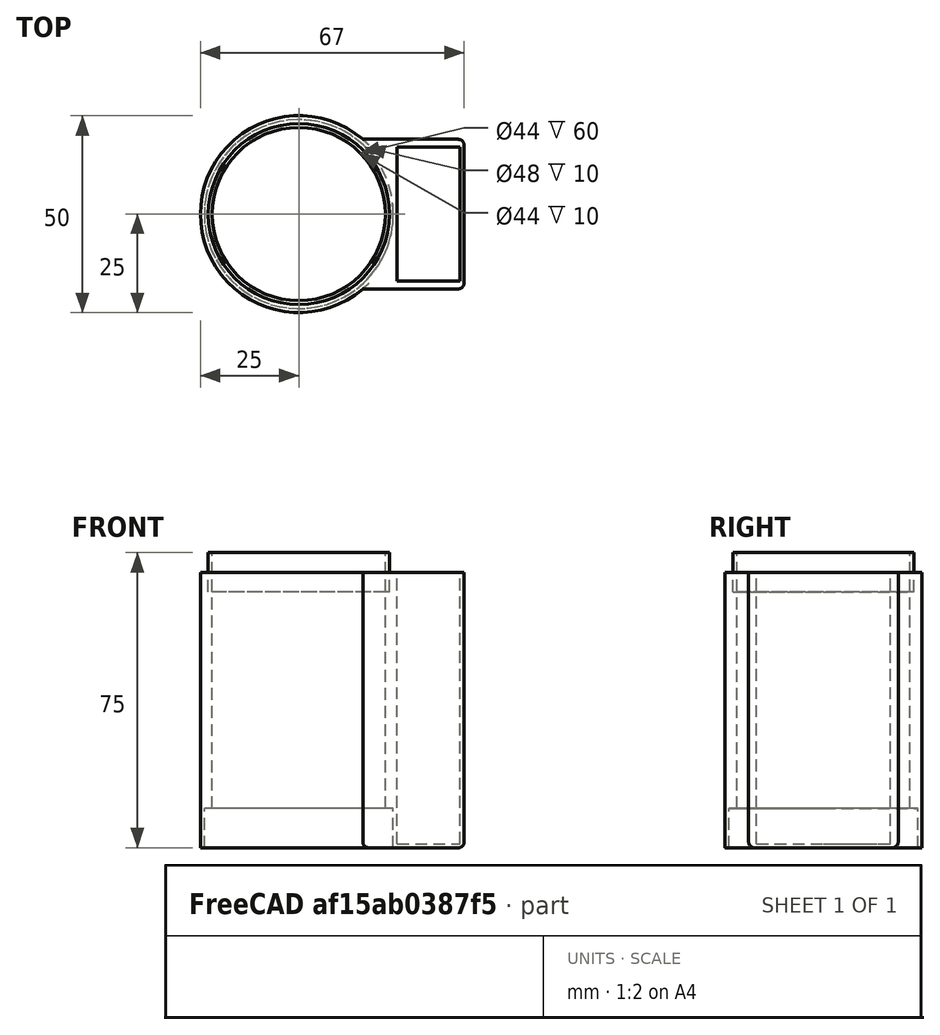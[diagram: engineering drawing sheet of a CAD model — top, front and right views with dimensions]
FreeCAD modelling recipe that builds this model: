
FCSTD DOCUMENT  (FreeCAD 0.15R4671 (Git))
Label: Mid section
License: CC-BY 3.0
LicenseURL: http://creativecommons.org/licenses/by/3.0/
objects: Part::Cylinder×5, Part::Cut×4, Part::Box×2, App::MeasureDistance×1, Part::Fillet×1, Part::MultiFuse×1
note: 13 computed .brp shape members not serialized (recipe doc carries the construction recipe); baked Part::Feature solids carry a one-line shape summary decoded from their .brp

FEATURE [Part::Cylinder] Cylinder  label="Cilindro"
  Angle = 360
  Height = 70
  Radius = 25
FEATURE [Part::Cylinder] Cylinder001  label="Cilindro001"
  Angle = 360
  Height = 78
  Radius = 22
FEATURE [Part::Cylinder] Cylinder003  label="Cilindro003"
  Angle = 360
  Height = 10
  Radius = 24
FEATURE [Part::Cylinder] Cylinder005  label="Cilindro005"
  Angle = 360
  Height = 21
  Radius = 22
FEATURE [Part::Cylinder] Cylinder006  label="Cilindro006"
  Angle = 360
  Height = 10
  Radius = 23
FEATURE [App::MeasureDistance] Distance  label="Distance: 70.087"
  Distance = 70.0868
  P1 = (-17.9835,17.3665,70)
  P2 = (-20.2254,14.6946,0)
FEATURE [Part::Box] Box  label="Cubo"
  Height = 70
  Length = 16
  Placement = pos=(25,-17,1) rot=(0,0,1;0rad)
  Width = 34
FEATURE [Part::Box] Box001  label="Cubo001"
  Height = 70
  Length = 26
  Placement = pos=(16,-19,0) rot=(0,0,1;0rad)
  Width = 38
FEATURE [Part::Fillet] Fillet
  Base = -> Box001
  Edges = 5 edges r=1.5: [Edge5,Edge7,Edge8,Edge9,Edge11]
FEATURE [Part::Cut] Cut
  Base = -> Fillet
  Tool = -> Box
FEATURE [Part::MultiFuse] Fusion
  Shapes = -> [Cut,Cylinder]
FEATURE [Part::Cut] Cut003
  Base = -> Fusion
  Tool = -> Cylinder001
FEATURE [Part::Cut] Cut004
  Base = -> Cut003
  Tool = -> Cylinder003
FEATURE [Part::Cut] Cut005
  Base = -> Cylinder006
  Placement = pos=(0,0,65) rot=(0,0,1;0rad)
  Tool = -> Cylinder005
